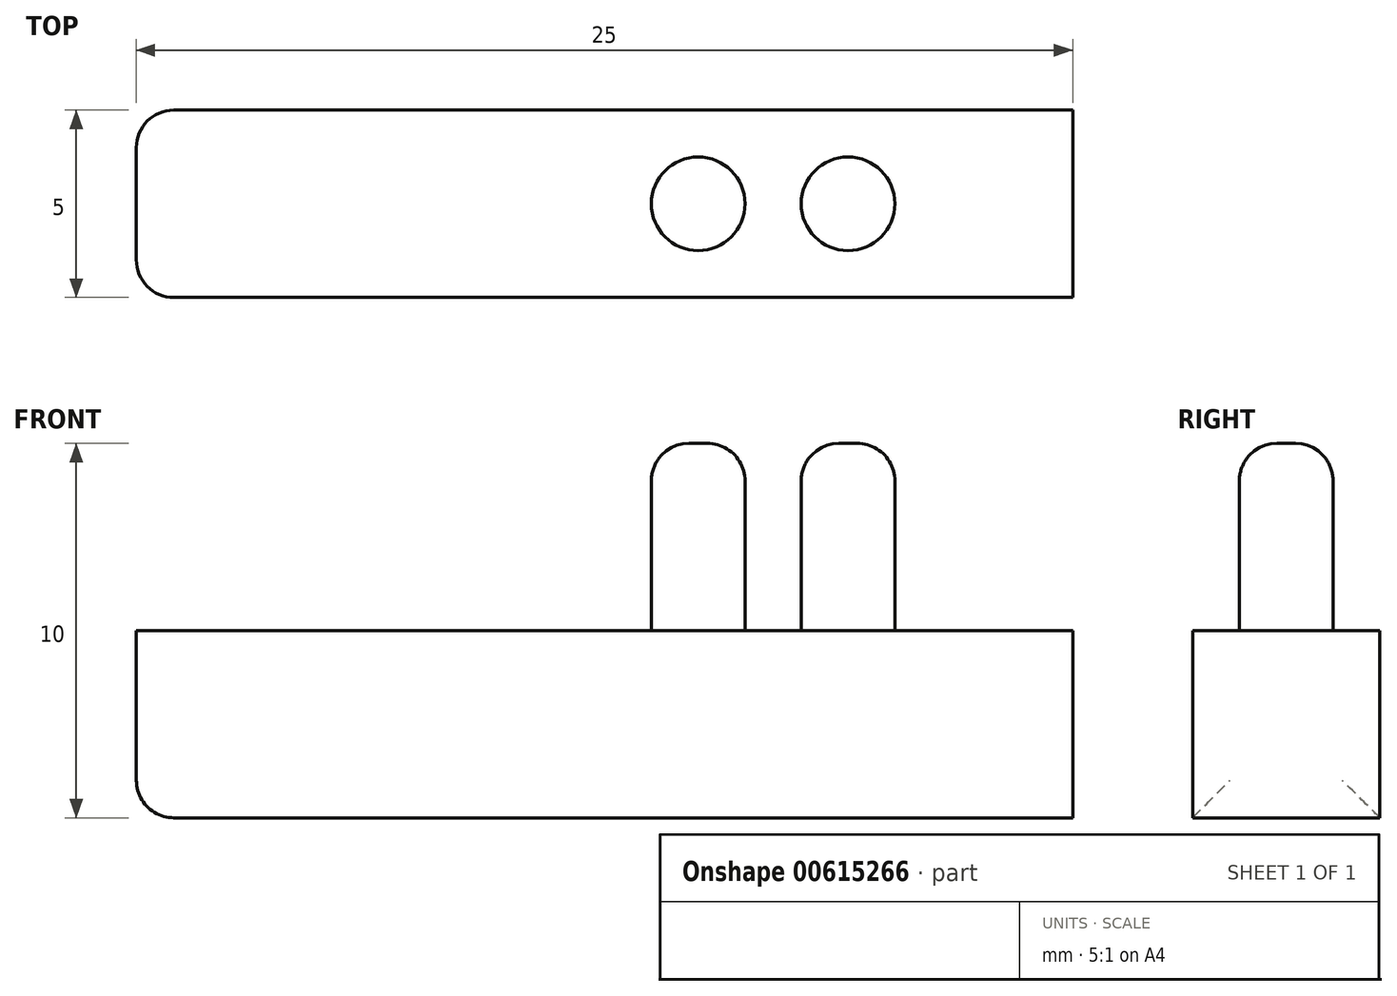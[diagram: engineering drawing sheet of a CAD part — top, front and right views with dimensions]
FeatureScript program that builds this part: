
annotation { "Feature Type Name" : "Feature", "Feature Type Description" : "" }
export const myFeature = defineFeature(function(context is Context, id is Id, definition is map)
    precondition{}
    {
        {
            var Q0;
            Q0=qCreatedBy(makeId("Top.planeOp"),FACE);
            var sketch = newSketch(context, id + "F0", { "sketchPlane" : qUnion([Q0])});
            skLineSegment(sketch, "E0.bottom", {"start": v(14.52, -2.5) * mm, "end": v(-10.48, -2.5) * mm});
            skLineSegment(sketch, "E0.top", {"start": v(14.52, 2.5) * mm, "end": v(-10.48, 2.5) * mm});
            skLineSegment(sketch, "E0.left", {"start": v(14.52, -2.5) * mm, "end": v(14.52, 2.5) * mm});
            skLineSegment(sketch, "E0.right", {"start": v(-10.48, -2.5) * mm, "end": v(-10.48, 2.5) * mm});
            skPoint(sketch, "E0.middle", {"position": v(2.02, 0) * mm});
            skLineSegment(sketch, "E1.bottom", {"start": v(-10.48, 2.5) * mm, "end": v(-8.23, 2.5) * mm, "construction": true});
            skLineSegment(sketch, "E1.top", {"start": v(-10.48, 0) * mm, "end": v(-8.23, 0) * mm, "construction": true});
            skLineSegment(sketch, "E1.left", {"start": v(-10.48, 2.5) * mm, "end": v(-10.48, 0) * mm, "construction": true});
            skLineSegment(sketch, "E1.right", {"start": v(-8.23, 2.5) * mm, "end": v(-8.23, 0) * mm, "construction": true});
            skLineSegment(sketch, "E2.bottom", {"start": v(-8.23, 2.5) * mm, "end": v(-4.73, 2.5) * mm, "construction": true});
            skLineSegment(sketch, "E2.top", {"start": v(-8.23, 0) * mm, "end": v(-4.73, 0) * mm, "construction": true});
            skLineSegment(sketch, "E2.right", {"start": v(-4.73, 2.5) * mm, "end": v(-4.73, 0) * mm, "construction": true});
            skLineSegment(sketch, "E3.bottom", {"start": v(-4.73, 2.5) * mm, "end": v(-1.48, 2.5) * mm, "construction": true});
            skLineSegment(sketch, "E3.top", {"start": v(-4.73, 0) * mm, "end": v(-1.48, 0) * mm, "construction": true});
            skLineSegment(sketch, "E3.right", {"start": v(-1.48, 2.5) * mm, "end": v(-1.48, 0) * mm, "construction": true});
            skLineSegment(sketch, "E4.bottom", {"start": v(-1.48, 2.5) * mm, "end": v(14.52, 2.5) * mm, "construction": true});
            skLineSegment(sketch, "E4.top", {"start": v(-1.48, 0) * mm, "end": v(14.52, 0) * mm, "construction": true});
            skLineSegment(sketch, "E4.right", {"start": v(14.52, 2.5) * mm, "end": v(14.52, 0) * mm, "construction": true});
            skCircle(sketch, "E5", {"center": v(-8.23, 0) * mm, "radius": 1.25 * mm, "construction": true});
            skCircle(sketch, "E6", {"center": v(-4.73, 0) * mm, "radius": 1.25 * mm, "construction": true});
            skSolve(sketch);
        }
        {
            var Q0;
            Q0=makeQuery(id+"F0.imprint","IMPRINT",FACE,{"disambiguationData":[TD([[makeQuery(id+"F0.imprint","IMPRINT",EDGE,{"derivedFrom":sQuery(id+"F0.wireOp",EDGE,"E0.bottom")}),-1.0]])]});
            extrude(context, id + "F1", {"entities" : qUnion([Q0]), "depth" : 5 * mm, "offsetDistance" : 25 * mm});
        }
        {
            var Q0;
            Q0=makeQuery(id+"F1.opExtrude","CAP_FACE",FACE,{"disambiguationData":[OSD([sQuery(id+"F0.wireOp",EDGE,"E0.bottom"),sQuery(id+"F0.wireOp",EDGE,"E0.top"),sQuery(id+"F0.wireOp",EDGE,"E0.left"),sQuery(id+"F0.wireOp",EDGE,"E0.right")])],"isStart":false});
            var sketch = newSketch(context, id + "F2", { "sketchPlane" : qUnion([Q0])});
            skLineSegment(sketch, "E7", {"start": v(14.52, 0) * mm, "end": v(8.52, 0) * mm, "construction": true});
            skPoint(sketch, "E7.endSnap0", {"position": v(14.52, 0) * mm});
            skLineSegment(sketch, "E8", {"start": v(8.52, 0) * mm, "end": v(4.52, 0) * mm, "construction": true});
            skCircle(sketch, "E9", {"center": v(4.52, 0) * mm, "radius": 1.25 * mm});
            skCircle(sketch, "E10", {"center": v(8.52, 0) * mm, "radius": 1.25 * mm});
            skLineSegment(sketch, "E11", {"start": v(4.52, 0) * mm, "end": v(0.52, 0) * mm, "construction": true});
            skLineSegment(sketch, "E12", {"start": v(0.52, 0) * mm, "end": v(-3.48, 0) * mm, "construction": true});
            skLineSegment(sketch, "E13", {"start": v(-3.48, 0) * mm, "end": v(-7.48, 0) * mm, "construction": true});
            skLineSegment(sketch, "E14", {"start": v(-7.48, 0) * mm, "end": v(-11.48, 0) * mm, "construction": true});
            skSolve(sketch);
        }
        {
            var Q0;
            Q0=makeQuery(id+"F2.imprint","IMPRINT",FACE,{"disambiguationData":[TD([[makeQuery(id+"F2.imprint","IMPRINT",EDGE,{"derivedFrom":sQuery(id+"F2.wireOp",EDGE,"E9")}),1.0]])]});
            var Q1;
            Q1=makeQuery(id+"F2.imprint","IMPRINT",FACE,{"disambiguationData":[TD([[makeQuery(id+"F2.imprint","IMPRINT",EDGE,{"derivedFrom":sQuery(id+"F2.wireOp",EDGE,"E10")}),1.0]])]});
            extrude(context, id + "F3", {"entities" : qUnion([Q0, Q1]), "operationType" : NewBodyOperationType.ADD, "depth" : 5 * mm, "offsetDistance" : 25 * mm});
        }
        {
            var Q0;
            Q0=makeQuery(id+"F1.opExtrude","SWEPT_EDGE",EDGE,{"disambiguationData":[OSD([sQuery(id+"F0.wireOp",EDGE,"E0.bottom"),sQuery(id+"F0.wireOp",EDGE,"E0.right")])]});
            var Q1;
            Q1=makeQuery(id+"F1.opExtrude","SWEPT_EDGE",EDGE,{"disambiguationData":[OSD([sQuery(id+"F0.wireOp",EDGE,"E0.top"),sQuery(id+"F0.wireOp",EDGE,"E0.right")])]});
            var Q2;
            Q2=makeQuery(id+"F3.opExtrude","CAP_FACE",FACE,{"disambiguationData":[OSD([sQuery(id+"F2.wireOp",EDGE,"E9")])],"isStart":false});
            var Q3;
            Q3=makeQuery(id+"F3.opExtrude","CAP_FACE",FACE,{"disambiguationData":[OSD([sQuery(id+"F2.wireOp",EDGE,"E10")])],"isStart":false});
            var Q4;
            Q4=makeQuery(id+"F1.opExtrude","CAP_EDGE",EDGE,{"disambiguationData":[OSD([sQuery(id+"F0.wireOp",EDGE,"E0.right")])],"isStart":true});
            fillet(context, id + "F4", {"entities" : qUnion([Q0, Q1, Q2, Q3, Q4]), "radius" : 1 * mm, "tangentPropagation" : true, "allowEdgeOverflow" : false});
        }
    });
